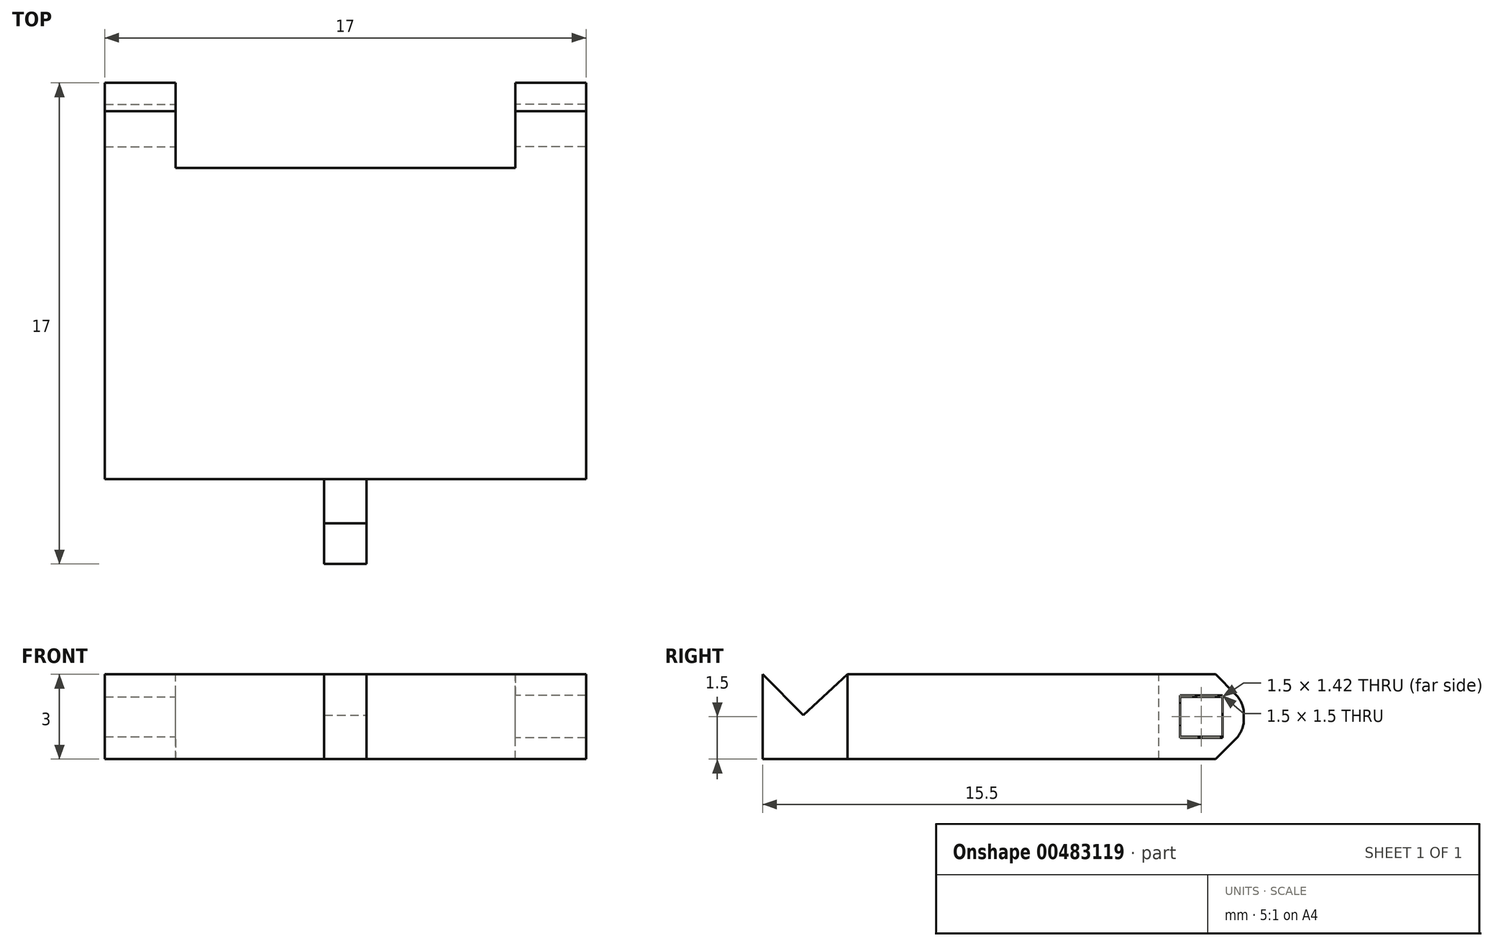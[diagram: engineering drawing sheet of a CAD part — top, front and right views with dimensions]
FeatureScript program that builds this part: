
annotation { "Feature Type Name" : "Feature", "Feature Type Description" : "" }
export const myFeature = defineFeature(function(context is Context, id is Id, definition is map)
    precondition{}
    {
        {
            var Q0;
            Q0=qCreatedBy(makeId("Top.planeOp"),FACE);
            var sketch = newSketch(context, id + "F0", { "sketchPlane" : qUnion([Q0])});
            skLineSegment(sketch, "E0.bottom", {"start": v(8.5, -5.5) * mm, "end": v(-8.5, -5.5) * mm});
            skLineSegment(sketch, "E0.top", {"start": v(8.5, 5.5) * mm, "end": v(-8.5, 5.5) * mm});
            skLineSegment(sketch, "E0.left", {"start": v(8.5, -5.5) * mm, "end": v(8.5, 5.5) * mm});
            skLineSegment(sketch, "E0.right", {"start": v(-8.5, -5.5) * mm, "end": v(-8.5, 5.5) * mm});
            skPoint(sketch, "E0.middle", {"position": v(0, 0) * mm});
            skSolve(sketch);
        }
        {
            var Q0;
            Q0 = qSketchRegion(id + "F0", true);
            extrude(context, id + "F1", {"entities" : qUnion([Q0]), "depth" : 3 * mm});
        }
        {
            var Q0;
            Q0=makeQuery(id+"F1.opExtrude","CAP_FACE",FACE,{"disambiguationData":[OSD([sQuery(id+"F0.wireOp",EDGE,"E0.bottom"),sQuery(id+"F0.wireOp",EDGE,"E0.top"),sQuery(id+"F0.wireOp",EDGE,"E0.left"),sQuery(id+"F0.wireOp",EDGE,"E0.right")])],"isStart":false});
            var sketch = newSketch(context, id + "F2", { "sketchPlane" : qUnion([Q0])});
            skLineSegment(sketch, "E1", {"start": v(8.5, 2.5) * mm, "end": v(-8.5, 2.5) * mm});
            skLineSegment(sketch, "E2", {"start": v(-6, 2.5) * mm, "end": v(-6, 5.5) * mm});
            skLineSegment(sketch, "E3", {"start": v(6, 2.5) * mm, "end": v(6, 5.5) * mm});
            skSolve(sketch);
        }
        {
            var Q0;
            {var subQ0=sQuery(id+"F2.wireOp",EDGE,"E2");Q0=makeQuery(id+"F2.imprint","IMPRINT",FACE,{"disambiguationData":[TD([[makeQuery(id+"F2.imprint","IMPRINT",EDGE,{"derivedFrom":subQ0}),-1.0]])]});}
            extrude(context, id + "F3", {"entities" : qUnion([Q0]), "operationType" : NewBodyOperationType.REMOVE, "endBound" : BoundingType.THROUGH_ALL, "oppositeDirection" : true, "depth" : 25 * mm});
        }
        {
            var Q0;
            Q0=makeQuery(id+"F3.boolean.opBoolean","COPY",FACE,{"derivedFrom":makeQuery(id+"F3.opExtrude","SWEPT_FACE",FACE,{"disambiguationData":[OSD([sQuery(id+"F2.wireOp",EDGE,"E3")])]})});
            var sketch = newSketch(context, id + "F4", { "sketchPlane" : qUnion([Q0])});
            skLineSegment(sketch, "E4.bottom", {"start": v(-4.75, 0.75) * mm, "end": v(-3.25, 0.75) * mm});
            skLineSegment(sketch, "E4.top", {"start": v(-4.75, 2.25) * mm, "end": v(-3.25, 2.25) * mm});
            skLineSegment(sketch, "E4.left", {"start": v(-4.75, 0.75) * mm, "end": v(-4.75, 2.25) * mm});
            skLineSegment(sketch, "E4.right", {"start": v(-3.25, 0.75) * mm, "end": v(-3.25, 2.25) * mm});
            skPoint(sketch, "E4.middle", {"position": v(-4, 1.5) * mm});
            skPoint(sketch, "E4.middle.positionSnap0", {"position": v(-5.5, 1.5) * mm});
            skPoint(sketch, "E4.middle.positionSnap1", {"position": v(-4, 3) * mm});
            skPoint(sketch, "E4.centerSnap0", {"position": v(-5.5, 1.5) * mm});
            skPoint(sketch, "E4.centerSnap1", {"position": v(-4, 3) * mm});
            skSolve(sketch);
        }
        {
            var Q0;
            Q0=makeQuery(id+"F4.imprint","IMPRINT",FACE,{"disambiguationData":[TD([[makeQuery(id+"F4.imprint","IMPRINT",EDGE,{"derivedFrom":sQuery(id+"F4.wireOp",EDGE,"E4.bottom")}),1.0]])]});
            extrude(context, id + "F5", {"entities" : qUnion([Q0]), "operationType" : NewBodyOperationType.REMOVE, "oppositeDirection" : true, "depth" : 100 * mm});
        }
        {
            var Q0;
            Q0=makeQuery(id+"F1.opExtrude","CAP_EDGE",EDGE,{"disambiguationData":[OSD([sQuery(id+"F0.wireOp",EDGE,"E0.top")])],"isStart":false});
            chamfer(context, id + "F6", {"entities" : qUnion([Q0]), "width" : 1 * mm, "tangentPropagation" : true});
        }
        {
            var Q0;
            Q0=makeQuery(id+"F1.opExtrude","CAP_EDGE",EDGE,{"disambiguationData":[OSD([sQuery(id+"F0.wireOp",EDGE,"E0.top")])],"isStart":true});
            chamfer(context, id + "F7", {"entities" : qUnion([Q0]), "width" : 1 * mm, "tangentPropagation" : true});
        }
        {
            var Q0;
            {var subQ0=sQuery(id+"F0.wireOp",EDGE,"E0.top");Q0=makeQuery(id+"F6.opChamfer","BLEND_EDGE",EDGE,{"blendedFrom":[makeQuery(id+"F1.opExtrude","CAP_EDGE",EDGE,{"disambiguationData":[OSD([subQ0])],"isStart":false}),makeQuery(id+"F1.opExtrude","SWEPT_FACE",FACE,{"disambiguationData":[OSD([subQ0])]})],"blendedInto":[makeQuery(id+"F1.opExtrude","SWEPT_FACE",FACE,{"disambiguationData":[OSD([subQ0])]})]});}
            var Q1;
            {var subQ0=sQuery(id+"F0.wireOp",EDGE,"E0.top");Q1=makeQuery(id+"F7.opChamfer","BLEND_EDGE",EDGE,{"blendedFrom":[makeQuery(id+"F1.opExtrude","CAP_EDGE",EDGE,{"disambiguationData":[OSD([subQ0])],"isStart":true}),makeQuery(id+"F1.opExtrude","SWEPT_FACE",FACE,{"disambiguationData":[OSD([subQ0])]})],"blendedInto":[makeQuery(id+"F1.opExtrude","SWEPT_FACE",FACE,{"disambiguationData":[OSD([subQ0])]})]});}
            fillet(context, id + "F8", {"entities" : qUnion([Q0, Q1]), "radius" : 1 * mm, "tangentPropagation" : true, "allowEdgeOverflow" : false});
        }
        {
            var Q0;
            Q0=makeQuery(id+"F1.opExtrude","SWEPT_FACE",FACE,{"disambiguationData":[OSD([sQuery(id+"F0.wireOp",EDGE,"E0.bottom")])]});
            extrude(context, id + "F9", {"entities" : qUnion([Q0]), "operationType" : NewBodyOperationType.ADD, "depth" : 3 * mm});
        }
        {
            var Q0;
            Q0=makeQuery(id+"F9.opExtrude","CAP_FACE",FACE,{"disambiguationData":[OSD([sQuery(id+"F0.wireOp",EDGE,"E0.bottom")])],"isStart":false});
            var sketch = newSketch(context, id + "F10", { "sketchPlane" : qUnion([Q0])});
            skLineSegment(sketch, "E5.bottom", {"start": v(0.75, 0) * mm, "end": v(-0.75, 0) * mm});
            skLineSegment(sketch, "E5.top", {"start": v(0.75, 3) * mm, "end": v(-0.75, 3) * mm});
            skLineSegment(sketch, "E5.left", {"start": v(0.75, 0) * mm, "end": v(0.75, 3) * mm});
            skLineSegment(sketch, "E5.right", {"start": v(-0.75, 0) * mm, "end": v(-0.75, 3) * mm});
            skPoint(sketch, "E5.middle", {"position": v(0, 1.5) * mm});
            skPoint(sketch, "E5.middle.positionSnap0", {"position": v(8.5, 1.5) * mm});
            skPoint(sketch, "E5.middle.positionSnap1", {"position": v(0, 3) * mm});
            skPoint(sketch, "E5.centerSnap0", {"position": v(8.5, 1.5) * mm});
            skPoint(sketch, "E5.centerSnap1", {"position": v(0, 3) * mm});
            skSolve(sketch);
        }
        {
            var Q0;
            Q0=makeQuery(id+"F10.imprint","IMPRINT",FACE,{"disambiguationData":[TD([[makeQuery(id+"F10.imprint","IMPRINT",EDGE,{"derivedFrom":sQuery(id+"F10.wireOp",EDGE,"E5.bottom")}),-1.0]])]});
            extrude(context, id + "F11", {"entities" : qUnion([Q0]), "operationType" : NewBodyOperationType.ADD, "depth" : 3 * mm});
        }
        {
            var Q0;
            Q0=makeQuery(id+"F11.opExtrude","SWEPT_FACE",FACE,{"disambiguationData":[OSD([sQuery(id+"F10.wireOp",EDGE,"E5.left")])]});
            var sketch = newSketch(context, id + "F12", { "sketchPlane" : qUnion([Q0])});
            skLineSegment(sketch, "E6", {"start": v(-11.5, 3) * mm, "end": v(-10.06, 1.55) * mm});
            skLineSegment(sketch, "E7", {"start": v(-10.06, 1.55) * mm, "end": v(-8.5, 3) * mm});
            skSolve(sketch);
        }
        {
            var Q0;
            Q0=makeQuery(id+"F12.imprint","IMPRINT",FACE,{"disambiguationData":[TD([[makeQuery(id+"F12.imprint","IMPRINT",EDGE,{"derivedFrom":sQuery(id+"F12.wireOp",EDGE,"E6")}),1.0]])]});
            extrude(context, id + "F13", {"entities" : qUnion([Q0]), "operationType" : NewBodyOperationType.REMOVE, "endBound" : BoundingType.THROUGH_ALL, "oppositeDirection" : true, "depth" : 25 * mm});
        }
        {
            var Q0;
            Q0=makeQuery(id+"F3.boolean.opBoolean","COPY",FACE,{"derivedFrom":makeQuery(id+"F3.opExtrude","SWEPT_FACE",FACE,{"disambiguationData":[OSD([sQuery(id+"F2.wireOp",EDGE,"E2")])]})});
            var sketch = newSketch(context, id + "F14", { "sketchPlane" : qUnion([Q0])});
            skLineSegment(sketch, "E8.bottom", {"start": v(3.25, 0.8) * mm, "end": v(4.75, 0.8) * mm});
            skLineSegment(sketch, "E8.top", {"start": v(3.25, 2.2) * mm, "end": v(4.75, 2.2) * mm});
            skLineSegment(sketch, "E8.left", {"start": v(3.25, 0.8) * mm, "end": v(3.25, 2.2) * mm});
            skLineSegment(sketch, "E8.right", {"start": v(4.75, 0.8) * mm, "end": v(4.75, 2.2) * mm});
            skPoint(sketch, "E8.middle", {"position": v(4, 1.5) * mm});
            skSolve(sketch);
        }
        {
            var Q0;
            Q0=makeQuery(id+"F14.imprint","IMPRINT",FACE,{"disambiguationData":[TD([[makeQuery(id+"F14.imprint","IMPRINT",EDGE,{"derivedFrom":sQuery(id+"F14.wireOp",EDGE,"E8.bottom")}),1.0]])]});
            extrude(context, id + "F15", {"entities" : qUnion([Q0]), "operationType" : NewBodyOperationType.REMOVE, "oppositeDirection" : true, "depth" : 25 * mm});
        }
    });
